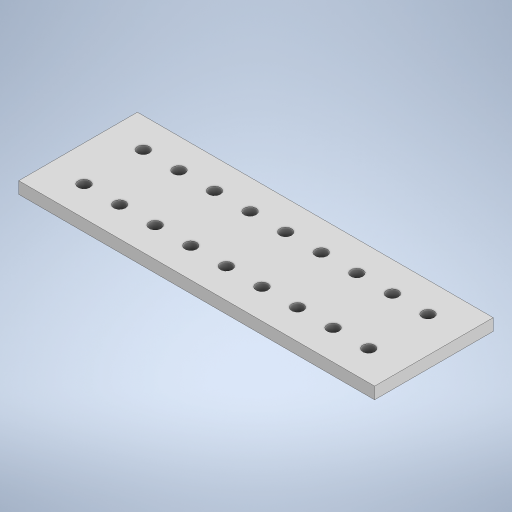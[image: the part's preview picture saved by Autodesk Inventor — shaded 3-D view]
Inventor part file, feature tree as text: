
AUTODESK INVENTOR PART (.ipt)
format: ipt  version: 2024 (Build 280153000, 153)  size: 253,952 bytes
history: native  units: mm
features: sketch x2, extrude x1, hole x1, pattern_linear x1
ambient origin geometry x8: Origin, YZ Plane, XZ Plane, XY Plane, X Axis, Y Axis, Z Axis, Center Point
bodies: Volumenkörper1 (feature_tree)
feature tree (5):
  extrude  "Extrusion1"  Depth=100.0mm
  hole  "Bohrung1"  [1 undecoded]
  pattern_linear  "Rechteckige Anordnung1"  Count1=3  [1 undecoded]
  sketch  "Skizze1"  dims[d0=300.0mm d1=100.0mm]
  sketch  "Skizze2"  dims[d2=10.0mm d3=0.0mm d4=25.0mm d5=30.0mm d6=10.0mm d7=6.0mm d8=2.5mm d9=0.75mm d10=90.0deg d11=8.0mm d12=20.594885mm d13=90.0mm d15=30.0mm d16=20.0mm d18=50.0mm]
note: 2 required parameter values undecoded (feature->parameter linkage not recoverable at this tier; creation-order binding heuristic only, values carry confidence <= 0.55)
